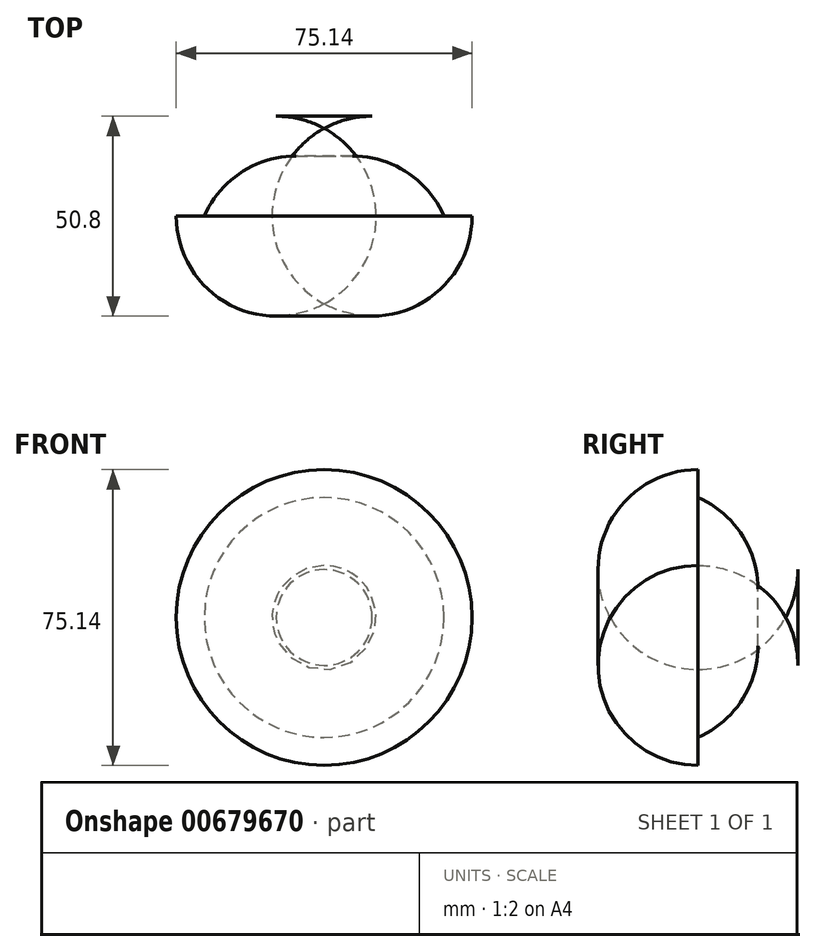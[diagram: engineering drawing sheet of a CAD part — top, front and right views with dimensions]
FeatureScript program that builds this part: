
annotation { "Feature Type Name" : "Feature", "Feature Type Description" : "" }
export const myFeature = defineFeature(function(context is Context, id is Id, definition is map)
    precondition{}
    {
        {
            var Q0;
            Q0=qCreatedBy(makeId("Front.planeOp"),FACE);
            var sketch = newSketch(context, id + "F0", { "sketchPlane" : qUnion([Q0])});
            skCircle(sketch, "E0", {"center": v(0, 0) * mm, "radius": 37.57 * mm});
            skArc(sketch, "E1", {"start": v(-38.59, -40.13) * mm, "mid": v(-28.05, -38.78) * mm, "end": v(-20.09, -31.75) * mm});
            skArc(sketch, "E2", {"start": v(-38.59, -40.13) * mm, "mid": v(-52.26, -43.58) * mm, "end": v(-60, -55.36) * mm});
            skArc(sketch, "E3.MirrorCS", {"start": v(38.59, -40.13) * mm, "mid": v(28.05, -38.78) * mm, "end": v(20.09, -31.75) * mm});
            skArc(sketch, "E4.MirrorCS", {"start": v(38.59, -40.13) * mm, "mid": v(52.26, -43.58) * mm, "end": v(60, -55.36) * mm});
            skSolve(sketch);
        }
        {
            var Q0;
            Q0=makeQuery(id+"F0.imprint","IMPRINT",FACE,{"disambiguationData":[TD([[makeQuery(id+"F0.imprint","IMPRINT",EDGE,{"derivedFrom":sQuery(id+"F0.wireOp",EDGE,"E0")}),1.0]])]});
            extrude(context, id + "F1", {"entities" : qUnion([Q0]), "depth" : 25.4 * mm, "offsetDistance" : 25.4 * mm});
        }
        {
            var Q0;
            Q0=makeQuery(id+"F1.opExtrude","CAP_EDGE",EDGE,{"disambiguationData":[OSD([sQuery(id+"F0.wireOp",EDGE,"E0")])],"isStart":true});
            fillet(context, id + "F2", {"entities" : qUnion([Q0]), "radius" : 25.4 * mm, "tangentPropagation" : true, "allowEdgeOverflow" : false});
        }
        {
            var Q0;
            Q0=makeQuery(id+"F1.opExtrude","CAP_FACE",FACE,{"disambiguationData":[OSD([sQuery(id+"F0.wireOp",EDGE,"E0")])],"isStart":false});
            var sketch = newSketch(context, id + "F3", { "sketchPlane" : qUnion([Q0])});
            skCircle(sketch, "E5", {"center": v(0, 0) * mm, "radius": 30.47 * mm});
            skSolve(sketch);
        }
        {
            var Q0;
            Q0=makeQuery(id+"F3.imprint","IMPRINT",FACE,{"disambiguationData":[TD([[makeQuery(id+"F3.imprint","IMPRINT",EDGE,{"derivedFrom":sQuery(id+"F3.wireOp",EDGE,"E5")}),1.0]])]});
            extrude(context, id + "F4", {"entities" : qUnion([Q0]), "operationType" : NewBodyOperationType.REMOVE, "oppositeDirection" : true, "depth" : 15.24 * mm, "offsetDistance" : 25.4 * mm});
        }
        {
            var Q0;
            Q0=makeQuery(id+"F4.boolean.opBoolean","COPY",EDGE,{"derivedFrom":makeQuery(id+"F4.opExtrude","CAP_EDGE",EDGE,{"disambiguationData":[OSD([sQuery(id+"F3.wireOp",EDGE,"E5")])],"isStart":false})});
            fillet(context, id + "F5", {"entities" : qUnion([Q0]), "radius" : 25.4 * mm, "tangentPropagation" : true, "allowEdgeOverflow" : false});
        }
    });
